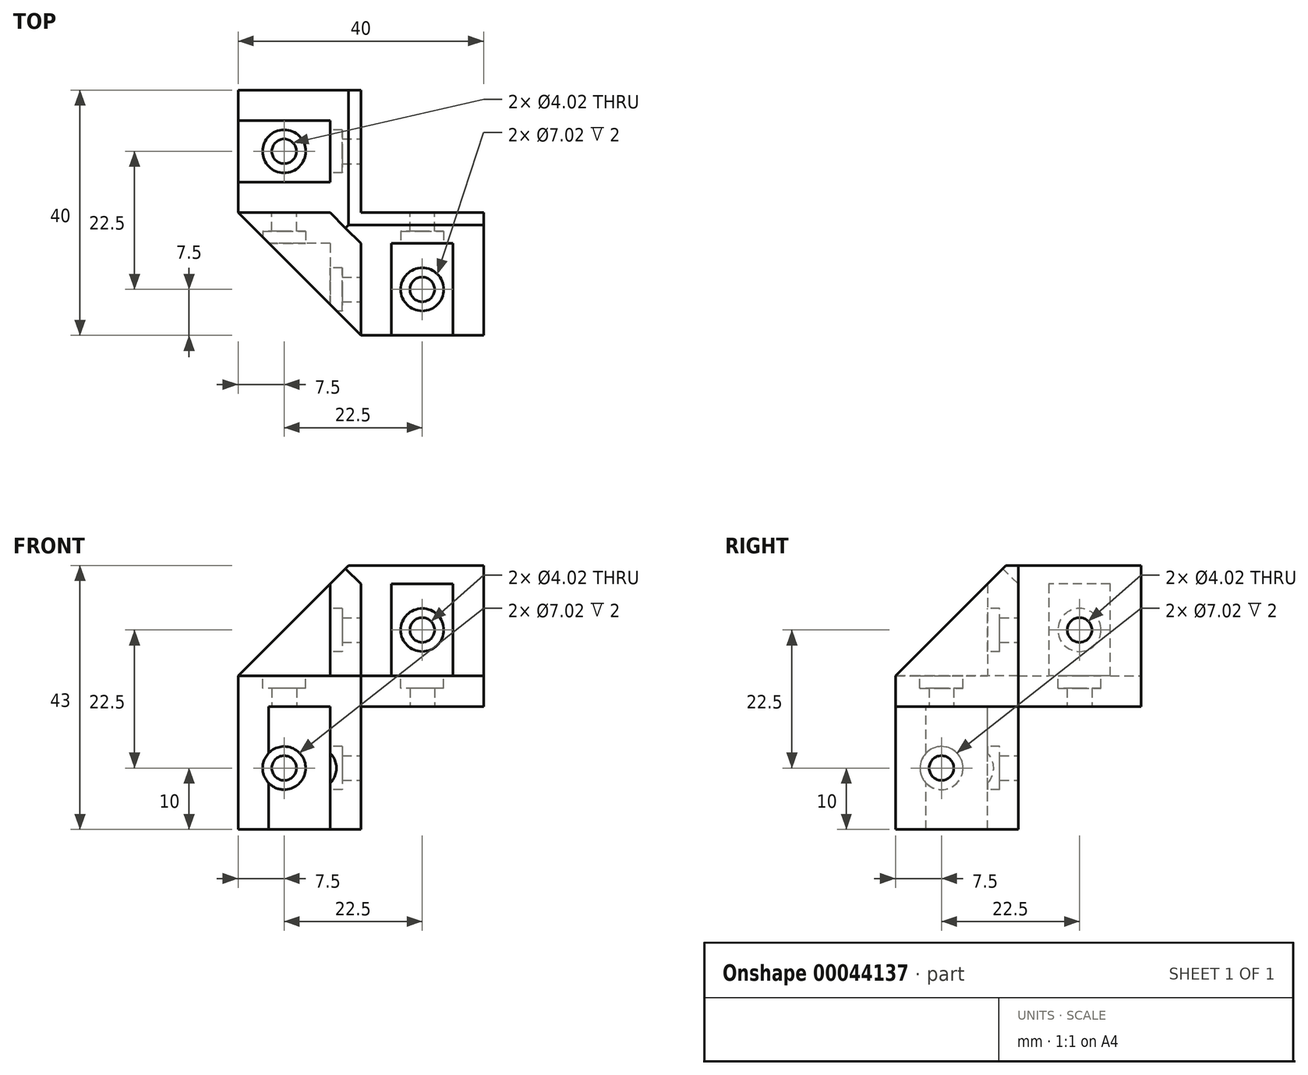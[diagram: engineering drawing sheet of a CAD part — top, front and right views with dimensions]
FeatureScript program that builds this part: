
annotation { "Feature Type Name" : "Feature", "Feature Type Description" : "" }
export const myFeature = defineFeature(function(context is Context, id is Id, definition is map)
    precondition{}
    {
        {
            var Q0;
            Q0=qCreatedBy(makeId("Top.planeOp"),FACE);
            var sketch = newSketch(context, id + "F0", { "sketchPlane" : qUnion([Q0])});
            skLineSegment(sketch, "E0", {"start": v(0, 0) * mm, "end": v(0, 20) * mm});
            skLineSegment(sketch, "E1", {"start": v(0, 20) * mm, "end": v(-20, 20) * mm});
            skLineSegment(sketch, "E2", {"start": v(-20, 20) * mm, "end": v(-20, 0) * mm});
            skLineSegment(sketch, "E3", {"start": v(-20, 0) * mm, "end": v(0, -20) * mm});
            skLineSegment(sketch, "E4", {"start": v(0, -20) * mm, "end": v(0, 0) * mm, "construction": true});
            skLineSegment(sketch, "E5", {"start": v(-20, 0) * mm, "end": v(0, 0) * mm, "construction": true});
            skLineSegment(sketch, "E6", {"start": v(0, 0) * mm, "end": v(20, 0) * mm});
            skLineSegment(sketch, "E7", {"start": v(20, 0) * mm, "end": v(20, -20) * mm});
            skLineSegment(sketch, "E8", {"start": v(20, -20) * mm, "end": v(0, -20) * mm});
            skSolve(sketch);
        }
        {
            var Q0;
            Q0 = qSketchRegion(id + "F0", true);
            extrude(context, id + "F1", {"entities" : qUnion([Q0]), "depth" : 5 * mm});
        }
        {
            var Q0;
            Q0=makeQuery(id+"F1.opExtrude","CAP_FACE",FACE,{"disambiguationData":[OSD([sQuery(id+"F0.wireOp",EDGE,"E0"),sQuery(id+"F0.wireOp",EDGE,"E1"),sQuery(id+"F0.wireOp",EDGE,"E2"),sQuery(id+"F0.wireOp",EDGE,"E3"),sQuery(id+"F0.wireOp",EDGE,"E6"),sQuery(id+"F0.wireOp",EDGE,"E7"),sQuery(id+"F0.wireOp",EDGE,"E8")])],"isStart":false});
            var sketch = newSketch(context, id + "F2", { "sketchPlane" : qUnion([Q0])});
            skLineSegment(sketch, "E9", {"start": v(20, -20) * mm, "end": v(20, 0) * mm});
            skLineSegment(sketch, "E10", {"start": v(20, 0) * mm, "end": v(0, 0) * mm});
            skLineSegment(sketch, "E11", {"start": v(0, 0) * mm, "end": v(0, 20) * mm});
            skLineSegment(sketch, "E12", {"start": v(0, 20) * mm, "end": v(-5, 20) * mm});
            skLineSegment(sketch, "E13", {"start": v(-5, 15) * mm, "end": v(-5, 5) * mm});
            skLineSegment(sketch, "E14", {"start": v(-5, 0) * mm, "end": v(0, -5) * mm});
            skLineSegment(sketch, "E15", {"start": v(0, -5) * mm, "end": v(0, -20) * mm});
            skLineSegment(sketch, "E16", {"start": v(0, -20) * mm, "end": v(5, -20) * mm});
            skLineSegment(sketch, "E17", {"start": v(5, -20) * mm, "end": v(5, -5) * mm});
            skLineSegment(sketch, "E18", {"start": v(5, -5) * mm, "end": v(15, -5) * mm});
            skLineSegment(sketch, "E19", {"start": v(15, -5) * mm, "end": v(15, -20) * mm});
            skLineSegment(sketch, "E20", {"start": v(15, -20) * mm, "end": v(20, -20) * mm});
            skLineSegment(sketch, "E21", {"start": v(-20, 15) * mm, "end": v(-5, 15) * mm});
            skLineSegment(sketch, "E22", {"start": v(-20, 5) * mm, "end": v(-5, 5) * mm});
            skLineSegment(sketch, "E23", {"start": v(-20, 0) * mm, "end": v(-5, 0) * mm});
            skLineSegment(sketch, "E24", {"start": v(-20, 15) * mm, "end": v(-20, 20) * mm});
            skLineSegment(sketch, "E25", {"start": v(-20, 20) * mm, "end": v(-5, 20) * mm});
            skLineSegment(sketch, "E26", {"start": v(-20, 0) * mm, "end": v(-20, 5) * mm});
            skLineSegment(sketch, "E27", {"start": v(-5, 0) * mm, "end": v(0, 0) * mm, "construction": true});
            skLineSegment(sketch, "E28", {"start": v(0, -5) * mm, "end": v(0, 0) * mm, "construction": true});
            skSolve(sketch);
        }
        {
            var Q0;
            Q0 = qSketchRegion(id + "F2", true);
            extrude(context, id + "F3", {"entities" : qUnion([Q0]), "operationType" : NewBodyOperationType.ADD, "depth" : 20 * mm});
        }
        {
            var Q0;
            Q0=makeQuery(id+"F3.boolean.opBoolean","MERGE",FACE,{"derivedFrom":[makeQuery(id+"F1.opExtrude","SWEPT_FACE",FACE,{"disambiguationData":[OSD([sQuery(id+"F0.wireOp",EDGE,"E7")])]}),makeQuery(id+"F3.opExtrude","SWEPT_FACE",FACE,{"disambiguationData":[OSD([sQuery(id+"F2.wireOp",EDGE,"E9")])]})]});
            var sketch = newSketch(context, id + "F4", { "sketchPlane" : qUnion([Q0])});
            skLineSegment(sketch, "E29", {"start": v(-10, 0) * mm, "end": v(-10, 5) * mm, "construction": true});
            skLineSegment(sketch, "E30", {"start": v(-10, 5) * mm, "end": v(-20, 5) * mm, "construction": true});
            skLineSegment(sketch, "E31", {"start": v(-10, 5) * mm, "end": v(0, 5) * mm, "construction": true});
            skLineSegment(sketch, "E32", {"start": v(0, 5) * mm, "end": v(0, 25) * mm, "construction": true});
            skLineSegment(sketch, "E33", {"start": v(0, 25) * mm, "end": v(-20, 5) * mm});
            skLineSegment(sketch, "E34", {"start": v(-20, 25) * mm, "end": v(-20, 5) * mm});
            skLineSegment(sketch, "E35", {"start": v(-20, 25) * mm, "end": v(0, 25) * mm});
            skSolve(sketch);
        }
        {
            var Q0;
            Q0=makeQuery(id+"F4.imprint","IMPRINT",FACE,{"disambiguationData":[TD([[makeQuery(id+"F4.imprint","IMPRINT",EDGE,{"derivedFrom":sQuery(id+"F4.wireOp",EDGE,"E33")}),-1.0]])]});
            extrude(context, id + "F5", {"entities" : qUnion([Q0]), "operationType" : NewBodyOperationType.REMOVE, "endBound" : BoundingType.THROUGH_ALL, "oppositeDirection" : true, "depth" : 25 * mm});
        }
        {
            var Q0;
            Q0=makeQuery(id+"F3.boolean.opBoolean","MERGE",FACE,{"derivedFrom":[makeQuery(id+"F1.opExtrude","SWEPT_FACE",FACE,{"disambiguationData":[OSD([sQuery(id+"F0.wireOp",EDGE,"E1")])]}),makeQuery(id+"F3.opExtrude","SWEPT_FACE",FACE,{"disambiguationData":[OSD([sQuery(id+"F2.wireOp",EDGE,"E12"),sQuery(id+"F2.wireOp",EDGE,"E25")])]})]});
            var sketch = newSketch(context, id + "F6", { "sketchPlane" : qUnion([Q0])});
            skLineSegment(sketch, "E36", {"start": v(10, 0) * mm, "end": v(10, 5) * mm, "construction": true});
            skLineSegment(sketch, "E37", {"start": v(10, 5) * mm, "end": v(0, 5) * mm, "construction": true});
            skLineSegment(sketch, "E38", {"start": v(0, 5) * mm, "end": v(0, 25) * mm, "construction": true});
            skLineSegment(sketch, "E39", {"start": v(10, 5) * mm, "end": v(20, 5) * mm, "construction": true});
            skLineSegment(sketch, "E40", {"start": v(20, 5) * mm, "end": v(0, 25) * mm});
            skLineSegment(sketch, "E41", {"start": v(20, 25) * mm, "end": v(0, 25) * mm});
            skLineSegment(sketch, "E42", {"start": v(20, 5) * mm, "end": v(20, 25) * mm});
            skSolve(sketch);
        }
        {
            var Q0;
            Q0=makeQuery(id+"F6.imprint","IMPRINT",FACE,{"disambiguationData":[TD([[makeQuery(id+"F6.imprint","IMPRINT",EDGE,{"derivedFrom":sQuery(id+"F6.wireOp",EDGE,"E40")}),-1.0]])]});
            extrude(context, id + "F7", {"entities" : qUnion([Q0]), "operationType" : NewBodyOperationType.REMOVE, "endBound" : BoundingType.THROUGH_ALL, "oppositeDirection" : true, "depth" : 25 * mm});
        }
        {
            var Q0;
            Q0=makeQuery(id+"F3.boolean.opBoolean","MERGE",FACE,{"derivedFrom":[makeQuery(id+"F1.opExtrude","SWEPT_FACE",FACE,{"disambiguationData":[OSD([sQuery(id+"F0.wireOp",EDGE,"E0")])]}),makeQuery(id+"F3.opExtrude","SWEPT_FACE",FACE,{"disambiguationData":[OSD([sQuery(id+"F2.wireOp",EDGE,"E11")])]})]});
            var sketch = newSketch(context, id + "F8", { "sketchPlane" : qUnion([Q0])});
            skCircle(sketch, "E43", {"center": v(10, 12.5) * mm, "radius": 2 * mm});
            skLineSegment(sketch, "E44", {"start": v(10, 12.5) * mm, "end": v(10, 0) * mm, "construction": true});
            skSolve(sketch);
        }
        {
            var Q0;
            Q0 = qSketchRegion(id + "F8", true);
            extrude(context, id + "F9", {"entities" : qUnion([Q0]), "operationType" : NewBodyOperationType.REMOVE, "oppositeDirection" : true, "depth" : 5 * mm});
        }
        {
            var Q0;
            Q0=makeQuery(id+"F3.boolean.opBoolean","MERGE",FACE,{"derivedFrom":[makeQuery(id+"F1.opExtrude","SWEPT_FACE",FACE,{"disambiguationData":[OSD([sQuery(id+"F0.wireOp",EDGE,"E6")])]}),makeQuery(id+"F3.opExtrude","SWEPT_FACE",FACE,{"disambiguationData":[OSD([sQuery(id+"F2.wireOp",EDGE,"E10")])]})]});
            var sketch = newSketch(context, id + "F10", { "sketchPlane" : qUnion([Q0])});
            skCircle(sketch, "E45", {"center": v(-10, 12.5) * mm, "radius": 2 * mm});
            skLineSegment(sketch, "E46", {"start": v(-10, 12.5) * mm, "end": v(-10, 0) * mm, "construction": true});
            skSolve(sketch);
        }
        {
            var Q0;
            Q0 = qSketchRegion(id + "F10", true);
            extrude(context, id + "F11", {"entities" : qUnion([Q0]), "operationType" : NewBodyOperationType.REMOVE, "oppositeDirection" : true, "depth" : 5 * mm});
        }
        {
            var Q0;
            Q0=makeQuery(id+"F3.opExtrude","SWEPT_FACE",FACE,{"disambiguationData":[OSD([sQuery(id+"F2.wireOp",EDGE,"E18")])]});
            var sketch = newSketch(context, id + "F12", { "sketchPlane" : qUnion([Q0])});
            skCircle(sketch, "E47", {"center": v(10, 12.5) * mm, "radius": 3.5 * mm});
            skSolve(sketch);
        }
        {
            var Q0;
            Q0 = qSketchRegion(id + "F12", true);
            extrude(context, id + "F13", {"entities" : qUnion([Q0]), "operationType" : NewBodyOperationType.REMOVE, "oppositeDirection" : true, "depth" : 2 * mm});
        }
        {
            var Q0;
            Q0=makeQuery(id+"F3.opExtrude","SWEPT_FACE",FACE,{"disambiguationData":[OSD([sQuery(id+"F2.wireOp",EDGE,"E13")])]});
            var sketch = newSketch(context, id + "F14", { "sketchPlane" : qUnion([Q0])});
            skCircle(sketch, "E48", {"center": v(-10, 12.5) * mm, "radius": 3.51 * mm});
            skSolve(sketch);
        }
        {
            var Q0;
            Q0 = qSketchRegion(id + "F14", true);
            extrude(context, id + "F15", {"entities" : qUnion([Q0]), "operationType" : NewBodyOperationType.REMOVE, "oppositeDirection" : true, "depth" : 2 * mm});
        }
        {
            var Q0;
            Q0=makeQuery(id+"F1.opExtrude","CAP_FACE",FACE,{"disambiguationData":[OSD([sQuery(id+"F0.wireOp",EDGE,"E0"),sQuery(id+"F0.wireOp",EDGE,"E1"),sQuery(id+"F0.wireOp",EDGE,"E2"),sQuery(id+"F0.wireOp",EDGE,"E3"),sQuery(id+"F0.wireOp",EDGE,"E6"),sQuery(id+"F0.wireOp",EDGE,"E7"),sQuery(id+"F0.wireOp",EDGE,"E8")])],"isStart":true});
            var sketch = newSketch(context, id + "F16", { "sketchPlane" : qUnion([Q0])});
            skCircle(sketch, "E49", {"center": v(-12.5, -10) * mm, "radius": 2 * mm});
            skCircle(sketch, "E50", {"center": v(10, 12.5) * mm, "radius": 2 * mm});
            skLineSegment(sketch, "E51", {"start": v(10, 0) * mm, "end": v(10, 12.5) * mm, "construction": true});
            skLineSegment(sketch, "E52", {"start": v(-12.5, -10) * mm, "end": v(0, -10) * mm, "construction": true});
            skSolve(sketch);
        }
        {
            var Q0;
            Q0 = qSketchRegion(id + "F16", true);
            extrude(context, id + "F17", {"entities" : qUnion([Q0]), "operationType" : NewBodyOperationType.REMOVE, "oppositeDirection" : true, "depth" : 5 * mm});
        }
        {
            var Q0;
            {var subQ0=sQuery(id+"F0.wireOp",EDGE,"E2");Q0=makeQuery(id+"F3.boolean.opBoolean","SPLIT",FACE,{"disambiguationData":[TD([makeQuery(id+"F3.opExtrude","SWEPT_FACE",FACE,{"disambiguationData":[OSD([sQuery(id+"F2.wireOp",EDGE,"E13")])]})])],"derivedFrom":makeQuery(id+"F1.opExtrude","CAP_FACE",FACE,{"disambiguationData":[OSD([sQuery(id+"F0.wireOp",EDGE,"E0"),sQuery(id+"F0.wireOp",EDGE,"E1"),subQ0,sQuery(id+"F0.wireOp",EDGE,"E3"),sQuery(id+"F0.wireOp",EDGE,"E6"),sQuery(id+"F0.wireOp",EDGE,"E7"),sQuery(id+"F0.wireOp",EDGE,"E8")])],"isStart":false})});}
            var sketch = newSketch(context, id + "F18", { "sketchPlane" : qUnion([Q0])});
            skCircle(sketch, "E53", {"center": v(-12.5, 10) * mm, "radius": 3.5 * mm});
            skSolve(sketch);
        }
        {
            var Q0;
            Q0 = qSketchRegion(id + "F18", true);
            extrude(context, id + "F19", {"entities" : qUnion([Q0]), "operationType" : NewBodyOperationType.REMOVE, "oppositeDirection" : true, "depth" : 2 * mm});
        }
        {
            var Q0;
            {var subQ0=sQuery(id+"F0.wireOp",EDGE,"E8");Q0=makeQuery(id+"F3.boolean.opBoolean","SPLIT",FACE,{"disambiguationData":[TD([makeQuery(id+"F3.opExtrude","SWEPT_FACE",FACE,{"disambiguationData":[OSD([sQuery(id+"F2.wireOp",EDGE,"E17")])]})])],"derivedFrom":makeQuery(id+"F1.opExtrude","CAP_FACE",FACE,{"disambiguationData":[OSD([sQuery(id+"F0.wireOp",EDGE,"E0"),sQuery(id+"F0.wireOp",EDGE,"E1"),sQuery(id+"F0.wireOp",EDGE,"E2"),sQuery(id+"F0.wireOp",EDGE,"E3"),sQuery(id+"F0.wireOp",EDGE,"E6"),sQuery(id+"F0.wireOp",EDGE,"E7"),subQ0])],"isStart":false})});}
            var sketch = newSketch(context, id + "F20", { "sketchPlane" : qUnion([Q0])});
            skCircle(sketch, "E54", {"center": v(10, -12.5) * mm, "radius": 3.5 * mm});
            skSolve(sketch);
        }
        {
            var Q0;
            Q0 = qSketchRegion(id + "F20", true);
            extrude(context, id + "F21", {"entities" : qUnion([Q0]), "operationType" : NewBodyOperationType.REMOVE, "oppositeDirection" : true, "depth" : 2 * mm});
        }
        {
            var Q0;
            Q0=qCreatedBy(makeId("Top.planeOp"),FACE);
            var sketch = newSketch(context, id + "F22", { "sketchPlane" : qUnion([Q0])});
            skLineSegment(sketch, "E55", {"start": v(0, 0) * mm, "end": v(-20, 0) * mm});
            skLineSegment(sketch, "E56", {"start": v(-20, 0) * mm, "end": v(-15, -5) * mm});
            skLineSegment(sketch, "E57", {"start": v(0, -20) * mm, "end": v(0, 0) * mm});
            skLineSegment(sketch, "E58", {"start": v(0, -10) * mm, "end": v(-5, -10) * mm, "construction": true});
            skLineSegment(sketch, "E59", {"start": v(-10, 0) * mm, "end": v(-10, -5) * mm, "construction": true});
            skLineSegment(sketch, "E60", {"start": v(-10, -5) * mm, "end": v(-5, -5) * mm});
            skLineSegment(sketch, "E61", {"start": v(-5, -5) * mm, "end": v(-5, -10) * mm});
            skLineSegment(sketch, "E62", {"start": v(-5, -10) * mm, "end": v(-5, -15) * mm});
            skLineSegment(sketch, "E63", {"start": v(-5, -15) * mm, "end": v(0, -20) * mm, "construction": true});
            skLineSegment(sketch, "E64", {"start": v(-10, -5) * mm, "end": v(-15, -5) * mm});
            skLineSegment(sketch, "E65.trimOffspring", {"start": v(-5, -15) * mm, "end": v(0, -20) * mm});
            skSolve(sketch);
        }
        {
            var Q0;
            Q0 = qSketchRegion(id + "F22", true);
            extrude(context, id + "F23", {"entities" : qUnion([Q0]), "operationType" : NewBodyOperationType.ADD, "oppositeDirection" : true, "depth" : 20 * mm});
        }
        {
            var Q0;
            Q0=makeQuery(id+"F23.opExtrude","SWEPT_FACE",FACE,{"disambiguationData":[OSD([sQuery(id+"F22.wireOp",EDGE,"E57")])]});
            var sketch = newSketch(context, id + "F24", { "sketchPlane" : qUnion([Q0])});
            skCircle(sketch, "E66", {"center": v(-12.5, -10) * mm, "radius": 2 * mm});
            skSolve(sketch);
        }
        {
            var Q0;
            Q0 = qSketchRegion(id + "F24", true);
            extrude(context, id + "F25", {"entities" : qUnion([Q0]), "operationType" : NewBodyOperationType.REMOVE, "oppositeDirection" : true, "depth" : 5 * mm});
        }
        {
            var Q0;
            Q0=makeQuery(id+"F23.opExtrude","SWEPT_FACE",FACE,{"disambiguationData":[OSD([sQuery(id+"F22.wireOp",EDGE,"E55")])]});
            var sketch = newSketch(context, id + "F26", { "sketchPlane" : qUnion([Q0])});
            skCircle(sketch, "E67", {"center": v(12.5, -10) * mm, "radius": 2 * mm});
            skSolve(sketch);
        }
        {
            var Q0;
            Q0 = qSketchRegion(id + "F26", true);
            extrude(context, id + "F27", {"entities" : qUnion([Q0]), "operationType" : NewBodyOperationType.REMOVE, "oppositeDirection" : true, "depth" : 5 * mm});
        }
        {
            var Q0;
            Q0=makeQuery(id+"F23.opExtrude","SWEPT_FACE",FACE,{"disambiguationData":[OSD([sQuery(id+"F22.wireOp",EDGE,"E61"),sQuery(id+"F22.wireOp",EDGE,"E62")])]});
            var sketch = newSketch(context, id + "F28", { "sketchPlane" : qUnion([Q0])});
            skCircle(sketch, "E68", {"center": v(12.5, -10) * mm, "radius": 3.5 * mm});
            skSolve(sketch);
        }
        {
            var Q0;
            Q0 = qSketchRegion(id + "F28", true);
            extrude(context, id + "F29", {"entities" : qUnion([Q0]), "operationType" : NewBodyOperationType.REMOVE, "oppositeDirection" : true, "depth" : 2 * mm});
        }
        {
            var Q0;
            Q0=makeQuery(id+"F23.opExtrude","SWEPT_FACE",FACE,{"disambiguationData":[OSD([sQuery(id+"F22.wireOp",EDGE,"E60"),sQuery(id+"F22.wireOp",EDGE,"E64")])]});
            var sketch = newSketch(context, id + "F30", { "sketchPlane" : qUnion([Q0])});
            skCircle(sketch, "E69", {"center": v(-12.5, -10) * mm, "radius": 3.5 * mm});
            skSolve(sketch);
        }
        {
            var Q0;
            Q0 = qSketchRegion(id + "F30", true);
            extrude(context, id + "F31", {"entities" : qUnion([Q0]), "operationType" : NewBodyOperationType.REMOVE, "oppositeDirection" : true, "depth" : 2 * mm});
        }
        {
            var Q0;
            Q0=makeQuery(id+"F3.boolean.opBoolean","MERGE",FACE,{"derivedFrom":[makeQuery(id+"F1.opExtrude","SWEPT_FACE",FACE,{"disambiguationData":[OSD([sQuery(id+"F0.wireOp",EDGE,"E6")])]}),makeQuery(id+"F3.opExtrude","SWEPT_FACE",FACE,{"disambiguationData":[OSD([sQuery(id+"F2.wireOp",EDGE,"E10")])]})]});
            var sketch = newSketch(context, id + "F32", { "sketchPlane" : qUnion([Q0])});
            skLineSegment(sketch, "E70", {"start": v(-20, 25) * mm, "end": v(-20, 23) * mm});
            skLineSegment(sketch, "E71", {"start": v(-20, 23) * mm, "end": v(0, 23) * mm});
            skLineSegment(sketch, "E72", {"start": v(0, 23) * mm, "end": v(0, 25) * mm});
            skLineSegment(sketch, "E73", {"start": v(0, 25) * mm, "end": v(-20, 25) * mm});
            skSolve(sketch);
        }
        {
            var Q0;
            Q0 = qSketchRegion(id + "F32", true);
            extrude(context, id + "F33", {"entities" : qUnion([Q0]), "operationType" : NewBodyOperationType.REMOVE, "endBound" : BoundingType.THROUGH_ALL, "oppositeDirection" : true, "depth" : 25 * mm});
        }
        {
            var Q0;
            Q0=makeQuery(id+"F33.boolean.opBoolean","MERGE",FACE,{"derivedFrom":[makeQuery(id+"F3.boolean.opBoolean","MERGE",FACE,{"derivedFrom":[makeQuery(id+"F1.opExtrude","SWEPT_FACE",FACE,{"disambiguationData":[OSD([sQuery(id+"F0.wireOp",EDGE,"E0")])]}),makeQuery(id+"F3.opExtrude","SWEPT_FACE",FACE,{"disambiguationData":[OSD([sQuery(id+"F2.wireOp",EDGE,"E11")])]})]}),makeQuery(id+"F33.opExtrude","SWEPT_FACE",FACE,{"disambiguationData":[OSD([sQuery(id+"F32.wireOp",EDGE,"E72")])]})]});
            var sketch = newSketch(context, id + "F34", { "sketchPlane" : qUnion([Q0])});
            skLineSegment(sketch, "E74", {"start": v(-2, 23) * mm, "end": v(20, 23) * mm});
            skLineSegment(sketch, "E75", {"start": v(20, 23) * mm, "end": v(20, 25) * mm});
            skLineSegment(sketch, "E76", {"start": v(20, 25) * mm, "end": v(-2.92, 25) * mm});
            skLineSegment(sketch, "E77", {"start": v(-2.92, 25) * mm, "end": v(-2.92, 22.9) * mm});
            skLineSegment(sketch, "E78", {"start": v(-2.92, 22.9) * mm, "end": v(-2, 23) * mm});
            skSolve(sketch);
        }
        {
            var Q0;
            Q0 = qSketchRegion(id + "F34", true);
            extrude(context, id + "F35", {"entities" : qUnion([Q0]), "operationType" : NewBodyOperationType.REMOVE, "endBound" : BoundingType.THROUGH_ALL, "oppositeDirection" : true, "depth" : 25 * mm});
        }
    });
